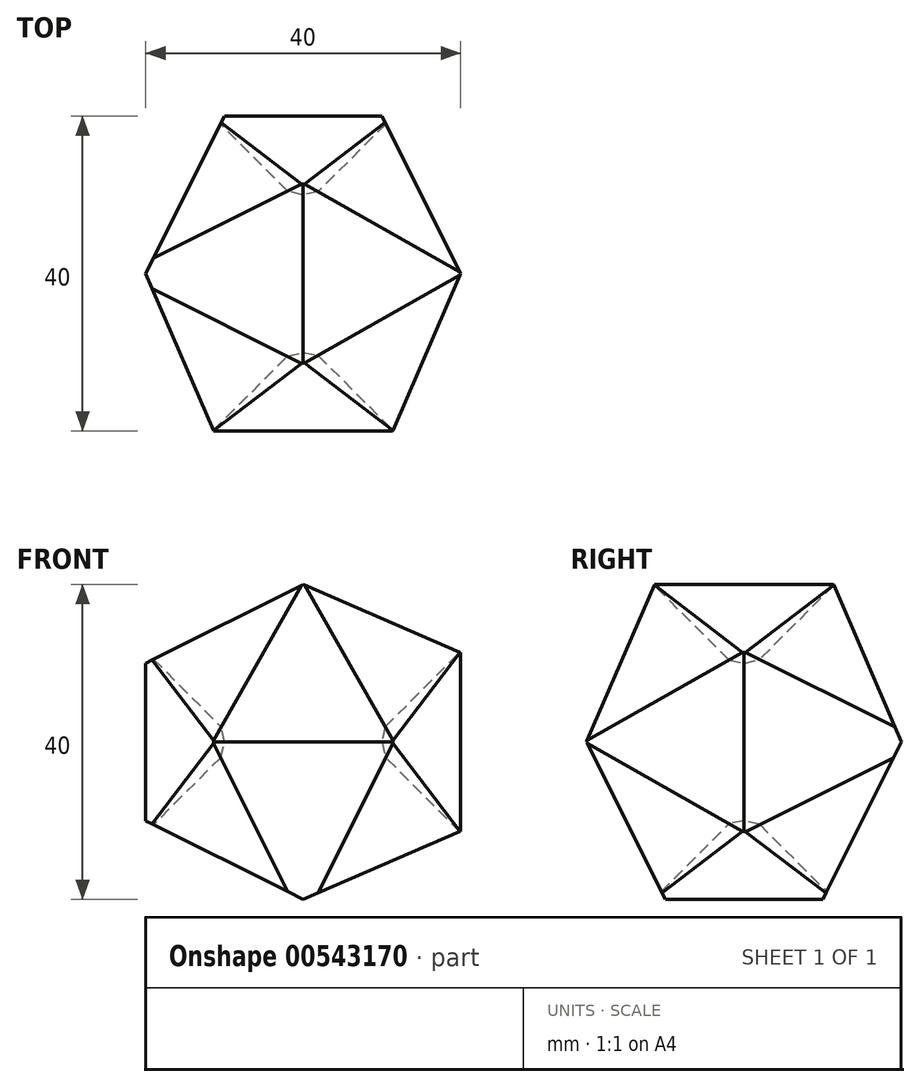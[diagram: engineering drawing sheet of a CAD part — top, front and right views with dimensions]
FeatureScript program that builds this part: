
annotation { "Feature Type Name" : "Feature", "Feature Type Description" : "" }
export const myFeature = defineFeature(function(context is Context, id is Id, definition is map)
    precondition{}
    {
        {
            var Q0;
            Q0=qCreatedBy(makeId("Front.planeOp"),FACE);
            var sketch = newSketch(context, id + "F0", { "sketchPlane" : qUnion([Q0])});
            skLineSegment(sketch, "E0", {"start": v(46.28, 0) * mm, "end": v(0, 20) * mm});
            skLineSegment(sketch, "E1", {"start": v(0, 20) * mm, "end": v(-40, 0) * mm});
            skLineSegment(sketch, "E2", {"start": v(-40, 0) * mm, "end": v(0, -20) * mm});
            skLineSegment(sketch, "E3", {"start": v(0, -20) * mm, "end": v(46.28, 0) * mm});
            skSolve(sketch);
        }
        {
            var Q0;
            Q0=makeQuery(id+"F0.imprint","IMPRINT",FACE,{"disambiguationData":[TD([[makeQuery(id+"F0.imprint","IMPRINT",EDGE,{"derivedFrom":sQuery(id+"F0.wireOp",EDGE,"E0")}),1.0]])]});
            extrude(context, id + "F1", {"entities" : qUnion([Q0]), "depth" : 25 * mm, "offsetDistance" : 25 * mm, "hasSecondDirection" : true, "secondDirectionOppositeDirection" : true, "secondDirectionDepth" : 25 * mm});
        }
        {
            var Q0;
            Q0=qCreatedBy(makeId("Front.planeOp"),FACE);
            var sketch = newSketch(context, id + "F2", { "sketchPlane" : qUnion([Q0])});
            skLineSegment(sketch, "E4", {"start": v(0, 49.78) * mm, "end": v(0, 0) * mm});
            skSolve(sketch);
        }
        {
            var Q0;
            Q0=qCreatedBy(makeId("Front.planeOp"),FACE);
            var sketch = newSketch(context, id + "F3", { "sketchPlane" : qUnion([Q0])});
            skLineSegment(sketch, "E5", {"start": v(60.84, 0) * mm, "end": v(0, 0) * mm});
            skSolve(sketch);
        }
        {
            var Q0;
            Q0=qCreatedBy(makeId("Right.planeOp"),FACE);
            var sketch = newSketch(context, id + "F4", { "sketchPlane" : qUnion([Q0])});
            skLineSegment(sketch, "E6", {"start": v(48.72, 0) * mm, "end": v(-1.84, 0) * mm});
            skSolve(sketch);
        }
        {
            var Q0;
            Q0=makeQuery(id+"F1.opExtrude","SWEPT_BODY",BODY,{"disambiguationData":[OSD([sQuery(id+"F0.wireOp",EDGE,"E0"),sQuery(id+"F0.wireOp",EDGE,"E1"),sQuery(id+"F0.wireOp",EDGE,"E2"),sQuery(id+"F0.wireOp",EDGE,"E3")])]});
            var Q1;
            Q1=sQuery(id+"F2.wireOp",EDGE,"E4");
            transform(context, id + "F5", {"entities" : qUnion([Q0]), "transformType" : TransformType.ROTATION, "transformAxis" : qUnion([Q1]), "angle" : 90 * degree, "makeCopy" : true});
        }
        {
            var Q0;
            Q0=makeQuery(id+"F5.opPattern","COPY",BODY,{"derivedFrom":makeQuery(id+"F1.opExtrude","SWEPT_BODY",BODY,{"disambiguationData":[OSD([sQuery(id+"F0.wireOp",EDGE,"E0"),sQuery(id+"F0.wireOp",EDGE,"E1"),sQuery(id+"F0.wireOp",EDGE,"E2"),sQuery(id+"F0.wireOp",EDGE,"E3")])]}),"instanceName":"1"});
            var Q1;
            Q1=sQuery(id+"F4.wireOp",EDGE,"E6");
            transform(context, id + "F6", {"entities" : qUnion([Q0]), "transformType" : TransformType.ROTATION, "transformAxis" : qUnion([Q1]), "angle" : 90 * degree, "makeCopy" : true});
        }
        {
            var Q0;
            Q0=makeQuery(id+"F5.opPattern","COPY",BODY,{"derivedFrom":makeQuery(id+"F1.opExtrude","SWEPT_BODY",BODY,{"disambiguationData":[OSD([sQuery(id+"F0.wireOp",EDGE,"E0"),sQuery(id+"F0.wireOp",EDGE,"E1"),sQuery(id+"F0.wireOp",EDGE,"E2"),sQuery(id+"F0.wireOp",EDGE,"E3")])]}),"instanceName":"1"});
            var Q1;
            Q1=sQuery(id+"F3.wireOp",EDGE,"E5");
            transform(context, id + "F7", {"entities" : qUnion([Q0]), "transformType" : TransformType.ROTATION, "transformAxis" : qUnion([Q1]), "angle" : 90 * degree, "makeCopy" : false});
        }
        {
            var Q0;
            Q0=makeQuery(id+"F5.opPattern","COPY",BODY,{"derivedFrom":makeQuery(id+"F1.opExtrude","SWEPT_BODY",BODY,{"disambiguationData":[OSD([sQuery(id+"F0.wireOp",EDGE,"E0"),sQuery(id+"F0.wireOp",EDGE,"E1"),sQuery(id+"F0.wireOp",EDGE,"E2"),sQuery(id+"F0.wireOp",EDGE,"E3")])]}),"instanceName":"1"});
            var Q1;
            Q1=makeQuery(id+"F6.opPattern","COPY",BODY,{"derivedFrom":makeQuery(id+"F5.opPattern","COPY",BODY,{"derivedFrom":makeQuery(id+"F1.opExtrude","SWEPT_BODY",BODY,{"disambiguationData":[OSD([sQuery(id+"F0.wireOp",EDGE,"E0"),sQuery(id+"F0.wireOp",EDGE,"E1"),sQuery(id+"F0.wireOp",EDGE,"E2"),sQuery(id+"F0.wireOp",EDGE,"E3")])]}),"instanceName":"1"}),"instanceName":"1"});
            booleanBodies(context, id + "F8", {"operationType" : BooleanOperationType.INTERSECTION, "tools" : qUnion([Q0, Q1])});
        }
        {
            var Q0;
            {var subQ0=makeQuery(id+"F5.opPattern","COPY",BODY,{"derivedFrom":makeQuery(id+"F1.opExtrude","SWEPT_BODY",BODY,{"disambiguationData":[OSD([sQuery(id+"F0.wireOp",EDGE,"E0"),sQuery(id+"F0.wireOp",EDGE,"E1"),sQuery(id+"F0.wireOp",EDGE,"E2"),sQuery(id+"F0.wireOp",EDGE,"E3")])]}),"instanceName":"1"});Q0=makeQuery(id+"F8.opBoolean","INTERSECT",BODY,{"derivedFrom":[subQ0,makeQuery(id+"F6.opPattern","COPY",BODY,{"derivedFrom":subQ0,"instanceName":"1"})]});}
            var Q1;
            Q1=makeQuery(id+"F1.opExtrude","SWEPT_BODY",BODY,{"disambiguationData":[OSD([sQuery(id+"F0.wireOp",EDGE,"E0"),sQuery(id+"F0.wireOp",EDGE,"E1"),sQuery(id+"F0.wireOp",EDGE,"E2"),sQuery(id+"F0.wireOp",EDGE,"E3")])]});
            booleanBodies(context, id + "F9", {"operationType" : BooleanOperationType.INTERSECTION, "tools" : qUnion([Q0, Q1])});
        }
        {
            var Q0;
            Q0=qCreatedBy(makeId("Top.planeOp"),FACE);
            var sketch = newSketch(context, id + "F10", { "sketchPlane" : qUnion([Q0])});
            skLineSegment(sketch, "E7", {"start": v(20, 0) * mm, "end": v(0, 20) * mm});
            skLineSegment(sketch, "E8", {"start": v(0, 20) * mm, "end": v(-20, 0) * mm});
            skLineSegment(sketch, "E9", {"start": v(-20, 0) * mm, "end": v(0, -20) * mm});
            skLineSegment(sketch, "E10", {"start": v(0, -20) * mm, "end": v(20, 0) * mm});
            skSolve(sketch);
        }
        {
            var Q0;
            Q0=qSketchRegion(id+"F10",true);
            extrude(context, id + "F11", {"entities" : qUnion([Q0]), "depth" : 20 * mm, "offsetDistance" : 25 * mm, "hasDraft" : true, "draftAngle" : atan(1 / sqrt(2)), "draftPullDirection" : true, "hasSecondDirection" : true, "secondDirectionOppositeDirection" : true, "secondDirectionDepth" : 20 * mm, "hasSecondDirectionDraft" : true, "secondDirectionDraftAngle" : atan(1 / sqrt(2)), "secondDirectionDraftPullDirection" : true});
        }
        {
            var Q0;
            {var subQ0=makeQuery(id+"F1.opExtrude","SWEPT_BODY",BODY,{"disambiguationData":[OSD([sQuery(id+"F0.wireOp",EDGE,"E0"),sQuery(id+"F0.wireOp",EDGE,"E1"),sQuery(id+"F0.wireOp",EDGE,"E2"),sQuery(id+"F0.wireOp",EDGE,"E3")])]});var subQ1=makeQuery(id+"F5.opPattern","COPY",BODY,{"derivedFrom":subQ0,"instanceName":"1"});Q0=makeQuery(id+"F9.opBoolean","INTERSECT",BODY,{"derivedFrom":[subQ0,makeQuery(id+"F8.opBoolean","INTERSECT",BODY,{"derivedFrom":[subQ1,makeQuery(id+"F6.opPattern","COPY",BODY,{"derivedFrom":subQ1,"instanceName":"1"})]})]});}
            transform(context, id + "F12", {"entities" : qUnion([Q0]), "transformType" : TransformType.TRANSLATION_3D, "dx" : 50 * mm, "dy" : 0 * mm, "dz" : 0 * mm, "makeCopy" : false});
        }
        {
            var Q0;
            Q0=makeQuery(id+"F11.*.split.splitOp","SPLIT",BODY,{"derivedFrom":makeQuery(id+"F11.opExtrude","SWEPT_BODY",BODY,{"disambiguationData":[OSD([sQuery(id+"F10.wireOp",EDGE,"E7"),sQuery(id+"F10.wireOp",EDGE,"E8"),sQuery(id+"F10.wireOp",EDGE,"E9"),sQuery(id+"F10.wireOp",EDGE,"E10")])]})});
            var Q1;
            Q1=qCreatedBy(makeId("Origin.pointOp"),VERTEX);
            transform(context, id + "F13", {"entities" : qUnion([Q0]), "transformType" : TransformType.SCALE_UNIFORMLY, "scale" : 1.5, "scalePoint" : qUnion([Q1]), "makeCopy" : false});
        }
        {
            var Q0;
            {var subQ0=makeQuery(id+"F1.opExtrude","SWEPT_BODY",BODY,{"disambiguationData":[OSD([sQuery(id+"F0.wireOp",EDGE,"E0"),sQuery(id+"F0.wireOp",EDGE,"E1"),sQuery(id+"F0.wireOp",EDGE,"E2"),sQuery(id+"F0.wireOp",EDGE,"E3")])]});var subQ1=makeQuery(id+"F5.opPattern","COPY",BODY,{"derivedFrom":subQ0,"instanceName":"1"});Q0=makeQuery(id+"F9.opBoolean","INTERSECT",BODY,{"derivedFrom":[subQ0,makeQuery(id+"F8.opBoolean","INTERSECT",BODY,{"derivedFrom":[subQ1,makeQuery(id+"F6.opPattern","COPY",BODY,{"derivedFrom":subQ1,"instanceName":"1"})]})]});}
            transform(context, id + "F14", {"entities" : qUnion([Q0]), "transformType" : TransformType.TRANSLATION_3D, "dx" : -50 * mm, "dy" : 0 * mm, "dz" : 0 * mm, "makeCopy" : false});
        }
        {
            var Q0;
            Q0=makeQuery(id+"F11.*.split.splitOp","SPLIT",BODY,{"derivedFrom":makeQuery(id+"F11.opExtrude","SWEPT_BODY",BODY,{"disambiguationData":[OSD([sQuery(id+"F10.wireOp",EDGE,"E7"),sQuery(id+"F10.wireOp",EDGE,"E8"),sQuery(id+"F10.wireOp",EDGE,"E9"),sQuery(id+"F10.wireOp",EDGE,"E10")])]})});
            var Q1;
            Q1=qCreatedBy(makeId("Origin.pointOp"),VERTEX);
            transform(context, id + "F15", {"entities" : qUnion([Q0]), "transformType" : TransformType.SCALE_UNIFORMLY, "scale" : 1.05, "scalePoint" : qUnion([Q1]), "makeCopy" : false});
        }
        {
            var Q0;
            Q0=makeQuery(id+"F11.*.split.splitOp","SPLIT",BODY,{"derivedFrom":makeQuery(id+"F11.opExtrude","SWEPT_BODY",BODY,{"disambiguationData":[OSD([sQuery(id+"F10.wireOp",EDGE,"E7"),sQuery(id+"F10.wireOp",EDGE,"E8"),sQuery(id+"F10.wireOp",EDGE,"E9"),sQuery(id+"F10.wireOp",EDGE,"E10")])]})});
            var Q1;
            {var subQ0=makeQuery(id+"F1.opExtrude","SWEPT_BODY",BODY,{"disambiguationData":[OSD([sQuery(id+"F0.wireOp",EDGE,"E0"),sQuery(id+"F0.wireOp",EDGE,"E1"),sQuery(id+"F0.wireOp",EDGE,"E2"),sQuery(id+"F0.wireOp",EDGE,"E3")])]});var subQ1=makeQuery(id+"F5.opPattern","COPY",BODY,{"derivedFrom":subQ0,"instanceName":"1"});Q1=makeQuery(id+"F9.opBoolean","INTERSECT",BODY,{"derivedFrom":[subQ0,makeQuery(id+"F8.opBoolean","INTERSECT",BODY,{"derivedFrom":[subQ1,makeQuery(id+"F6.opPattern","COPY",BODY,{"derivedFrom":subQ1,"instanceName":"1"})]})]});}
            booleanBodies(context, id + "F16", {"operationType" : BooleanOperationType.INTERSECTION, "tools" : qUnion([Q0, Q1])});
        }
    });
